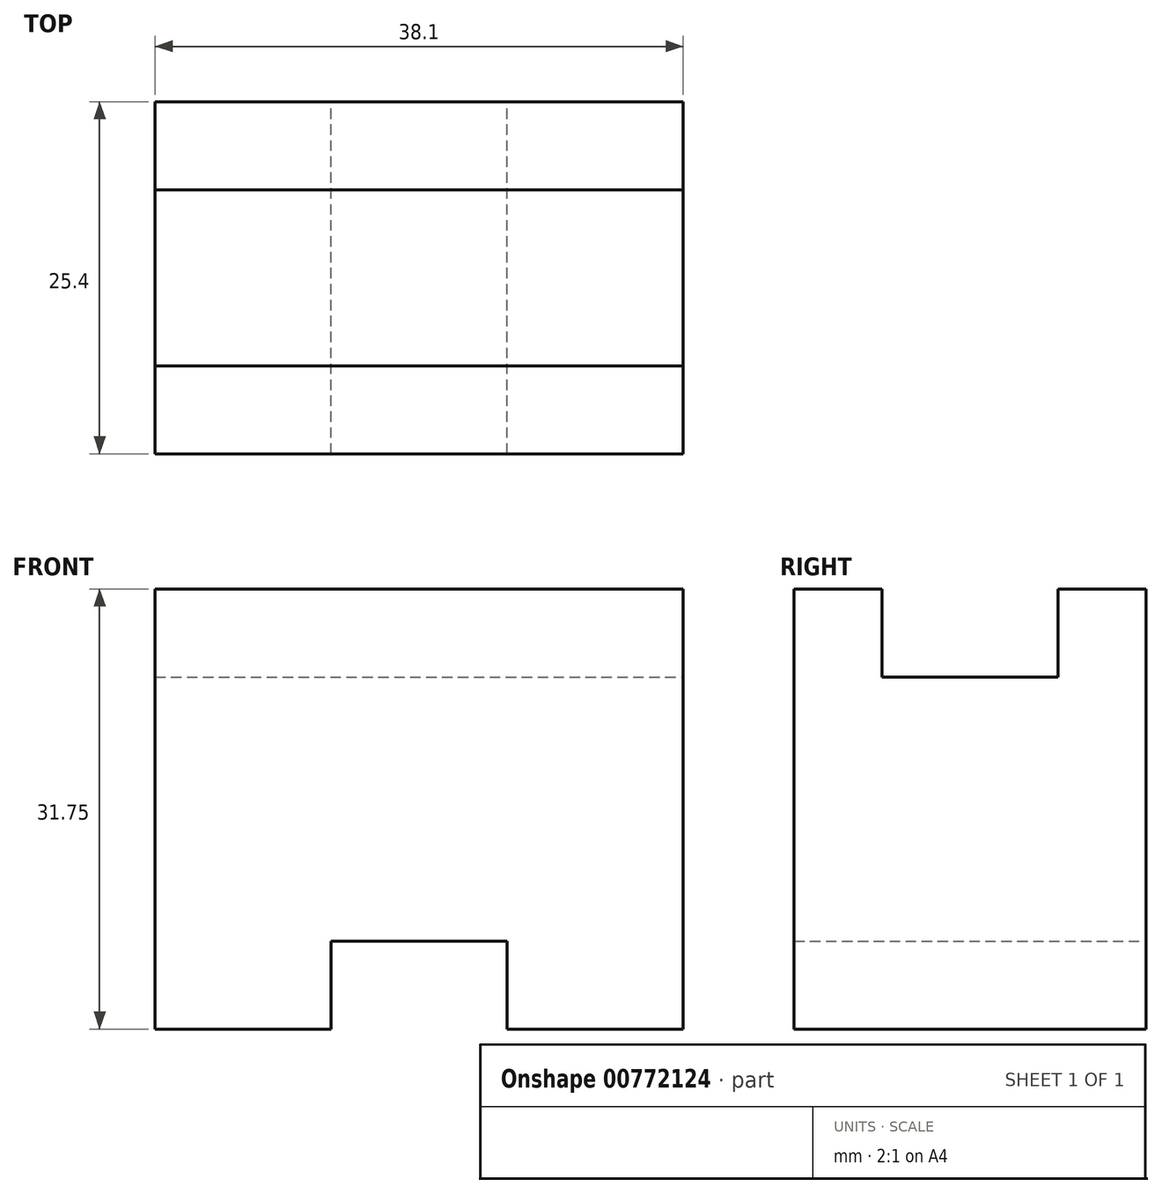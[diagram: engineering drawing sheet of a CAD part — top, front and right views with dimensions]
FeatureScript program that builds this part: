
annotation { "Feature Type Name" : "Feature", "Feature Type Description" : "" }
export const myFeature = defineFeature(function(context is Context, id is Id, definition is map)
    precondition{}
    {
        {
            var Q0;
            Q0=qCreatedBy(makeId("Front.planeOp"),FACE);
            var sketch = newSketch(context, id + "F0", { "sketchPlane" : qUnion([Q0])});
            skLineSegment(sketch, "E0", {"start": v(0, 0) * mm, "end": v(0, -31.75) * mm});
            skLineSegment(sketch, "E1", {"start": v(0, -31.75) * mm, "end": v(12.7, -31.75) * mm});
            skLineSegment(sketch, "E2", {"start": v(12.7, -31.75) * mm, "end": v(12.7, -25.4) * mm});
            skLineSegment(sketch, "E3", {"start": v(12.7, -25.4) * mm, "end": v(25.4, -25.4) * mm});
            skLineSegment(sketch, "E4", {"start": v(25.4, -25.4) * mm, "end": v(25.4, -31.75) * mm});
            skLineSegment(sketch, "E5", {"start": v(25.4, -31.75) * mm, "end": v(38.1, -31.75) * mm});
            skLineSegment(sketch, "E6", {"start": v(38.1, -31.75) * mm, "end": v(38.1, 0) * mm});
            skLineSegment(sketch, "E7", {"start": v(38.1, 0) * mm, "end": v(0, 0) * mm});
            skSolve(sketch);
        }
        {
            var Q0;
            Q0 = qSketchRegion(id + "F0", true);
            extrude(context, id + "F1", {"entities" : qUnion([Q0]), "depth" : 25.4 * mm, "offsetDistance" : 25.4 * mm});
        }
        {
            var Q0;
            Q0=makeQuery(id+"F1.opExtrude","SWEPT_FACE",FACE,{"disambiguationData":[OSD([sQuery(id+"F0.wireOp",EDGE,"E6")])]});
            var sketch = newSketch(context, id + "F2", { "sketchPlane" : qUnion([Q0])});
            skLineSegment(sketch, "E8", {"start": v(-25.4, 0) * mm, "end": v(-19.05, 0) * mm});
            skLineSegment(sketch, "E9", {"start": v(-19.05, 0) * mm, "end": v(-19.05, -6.35) * mm});
            skLineSegment(sketch, "E10", {"start": v(-19.05, -6.35) * mm, "end": v(-6.35, -6.35) * mm});
            skLineSegment(sketch, "E11", {"start": v(-6.35, -6.35) * mm, "end": v(-6.35, 0) * mm});
            skSolve(sketch);
        }
        {
            var Q0;
            {var subQ0=sQuery(id+"F2.wireOp",EDGE,"E9");Q0=makeQuery(id+"F2.imprint","IMPRINT",FACE,{"disambiguationData":[TD([[makeQuery(id+"F2.imprint","IMPRINT",EDGE,{"derivedFrom":subQ0}),1.0]])]});}
            extrude(context, id + "F3", {"entities" : qUnion([Q0]), "operationType" : NewBodyOperationType.REMOVE, "oppositeDirection" : true, "depth" : 38.1 * mm, "offsetDistance" : 25.4 * mm});
        }
    });
